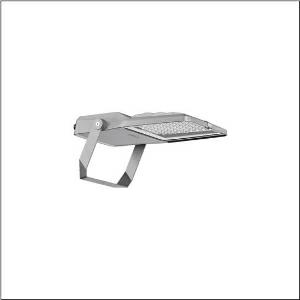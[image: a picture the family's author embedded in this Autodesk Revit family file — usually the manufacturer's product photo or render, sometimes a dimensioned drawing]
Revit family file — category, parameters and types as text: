
# Revit family: floodlight_fl_21_iq_mini___pl64_5xa7771b2e1a_713d
name_source: partatom
category: Lighting Fixtures
units: mm (PartAtom-declared; Revit-internal decimal feet)

## family parameters
Cut with Voids When Loaded = No
Host = Face
Light Source = No
Part Type = Normal
Room Calculation Point = No
Round Connector Dimension = Use Diameter
Shared = No

## types (1)
- --- (1 x LED, 6020 lm, 45.5 W, 3000K)
    Apparent Load = 46 VA
    CIE Flux Codes = 28 80 98 100 100
    Color Rendering = 70
    Color Temperature = 3000K
    Default Elevation = 1800 mm
    Description = Floodlight FL 21 iQ mini, floodlight, primary light control with lens, of PMMA, primary optical cover: protective disc, of toughened safety glass, transparent, light distribution: PL64, light emission: direct distribution, installation type: surface-mounted, LED, High Power LED, rated luminous flux: 6.020lm, luminous efficacy: 132lm/W, light colour: 730, colour temperature: 3000K, control gear: iQ Comfort/DALI, control: Auto-Match, Temp-Guard, Lumen-Switch, Night-Set, Smart-Wire, Light-Fading, Desk-Remote (wireless, voltage-free reading and setting of iQ features in the workshop via application-optimized NFC function/RFID function), optimised constant luminous flux control (CLO 2.0), with terminal, 6-pole, mains connection: 220..240V, AC, 50/60Hz, start of lifetime: 46W, end of service life: 48W, reduction: 22W, luminaire housing, of diecast aluminium, powder-coated, Siteco® metallic grey (DB 702S), corrosivity category C5 mid according to DIN EN ISO 12944, suitable for swimming pools, chlorine-resistant, sealing non-destructively replaceable, mounting bracket, of steel, galvanised, powder-coated, Siteco® metallic grey (DB 702S), protection rating (complete): IP66, insulation class (complete): insulation class II (safety insulation), certification: CE, ENEC, VDE, protection symbol: D, impact resistance: IK08, permissible operating ambient temperature: -40..+40°C, permissible operating ambient temperature for outdoor applications: -40..+50°C, standard: DIN EN 12944, LABS conformity tested according to VDMA 24364:2018-05, packaging unit: 1 piece

Light Distribution: PL64
    Height = 70 mm
    Lamp = 1 x LED
    Lamp Light Flux = 6020 lm
    Lamp Power = 45.5 W
    Lamp count = 1
    Length = 485 mm
    Luminous efficacy = 132 lm/W
    Manufacturer = Siteco
    ModVariant = No
    Model = 5XA7771B2E1A
    Mounting Place = Wall
    Mounting Type = Surface mounted
    Number of Poles = 1
    OnlyDefault = Yes
    Power Factor = 1
    Product Name = Floodlight FL 21 iQ mini | PL64
    Product group = floodlight | wall mounted
    ProductGroupID = 2001
    Protection Class = Protection class II
    Protection Degree = IP 66
    RLX_Detail_Level = 1
    RLX_Emergency_Light_Flux = 0 lm
    RLX_Emergency_Type = 0
    RLX_Emergency_Type_DB = No
    RlxData = <blob elided: 97137 chars, md5=e71cc1b7>
    Socket = socket
    Standby Power = 0 W
    System Light Flux = 6020 lm
    System Power = 46 W
    Type Comments = factory setting: luminous flux: 100 % | dim-lin: 254 | 463 mA
    Type Image = l_1006845.jpg
    URL = http://relux.com
    VarID = @adj_167226
    Voltage = 0 V
    Weight = 0.00 kg
    Width = 337 mm

## geometry (parser evidence)
native form markers: Blend x4, Sweep x13
no freeform markers — native parametric forms only
